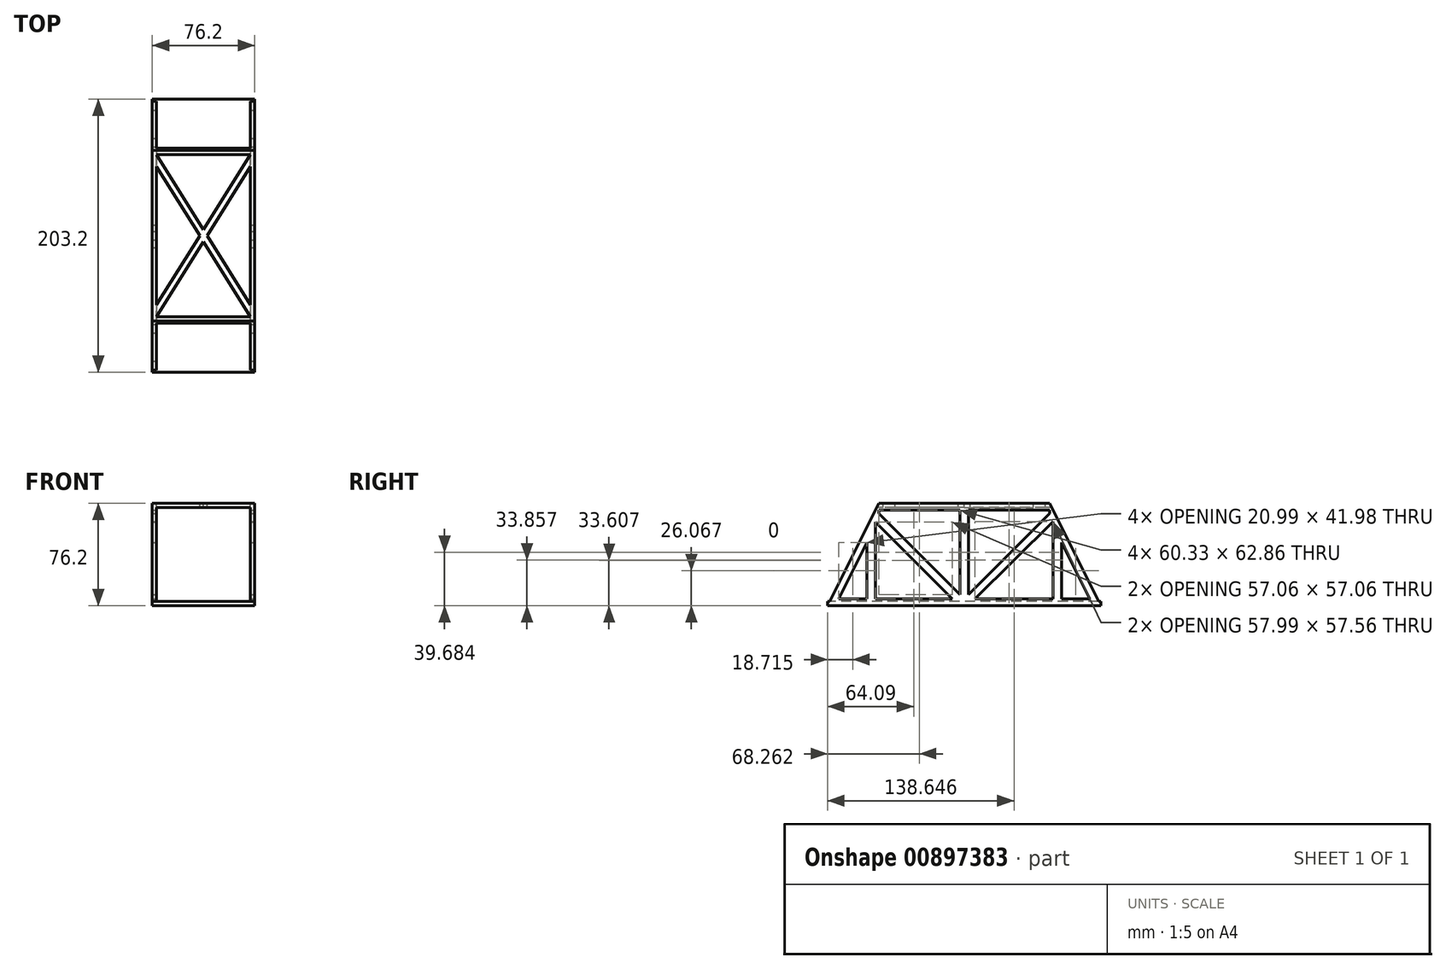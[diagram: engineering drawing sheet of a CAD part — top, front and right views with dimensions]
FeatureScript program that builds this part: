
annotation { "Feature Type Name" : "Feature", "Feature Type Description" : "" }
export const myFeature = defineFeature(function(context is Context, id is Id, definition is map)
    precondition{}
    {
        {
            var Q0;
            Q0=qCreatedBy(makeId("Right.planeOp"),FACE);
            var sketch = newSketch(context, id + "F0", { "sketchPlane" : qUnion([Q0])});
            skLineSegment(sketch, "E0", {"start": v(-101.6, -44.1) * mm, "end": v(101.6, -44.1) * mm});
            skLineSegment(sketch, "E1", {"start": v(-63.5, 32.1) * mm, "end": v(63.5, 32.1) * mm});
            skLineSegment(sketch, "E2", {"start": v(-101.6, -44.1) * mm, "end": v(-63.5, 32.1) * mm});
            skLineSegment(sketch, "E3", {"start": v(63.5, 32.1) * mm, "end": v(101.6, -44.1) * mm});
            skSolve(sketch);
        }
        {
            var Q0;
            Q0=makeQuery(id+"F0.imprint","IMPRINT",FACE,{"disambiguationData":[TD([[makeQuery(id+"F0.imprint","IMPRINT",EDGE,{"derivedFrom":sQuery(id+"F0.wireOp",EDGE,"E0")}),1.0]])]});
            extrude(context, id + "F1", {"entities" : qUnion([Q0]), "endBound" : BoundingType.SYMMETRIC, "depth" : 76.2 * mm, "offsetDistance" : 25.4 * mm});
        }
        {
            var Q0;
            Q0=qCreatedBy(makeId("Front.planeOp"),FACE);
            var sketch = newSketch(context, id + "F2", { "sketchPlane" : qUnion([Q0])});
            skLineSegment(sketch, "E4.bottom", {"start": v(34.92, -40.93) * mm, "end": v(-34.93, -40.93) * mm});
            skLineSegment(sketch, "E4.top", {"start": v(34.92, 28.92) * mm, "end": v(-34.92, 28.92) * mm});
            skLineSegment(sketch, "E4.left", {"start": v(34.93, -40.93) * mm, "end": v(34.93, 28.92) * mm});
            skLineSegment(sketch, "E4.right", {"start": v(-34.93, -40.93) * mm, "end": v(-34.93, 28.92) * mm});
            skPoint(sketch, "E4.middle", {"position": v(0, -6) * mm});
            skSolve(sketch);
        }
        {
            var Q0;
            Q0 = qSketchRegion(id + "F2", true);
            extrude(context, id + "F3", {"entities" : qUnion([Q0]), "operationType" : NewBodyOperationType.REMOVE, "endBound" : BoundingType.SYMMETRIC, "oppositeDirection" : true, "depth" : 254 * mm, "offsetDistance" : 25.4 * mm});
        }
        {
            var Q0;
            Q0=makeQuery(id+"F1.opExtrude","CAP_FACE",FACE,{"disambiguationData":[OSD([sQuery(id+"F0.wireOp",EDGE,"E0"),sQuery(id+"F0.wireOp",EDGE,"E1"),sQuery(id+"F0.wireOp",EDGE,"E2"),sQuery(id+"F0.wireOp",EDGE,"E3")])],"isStart":false});
            var sketch = newSketch(context, id + "F4", { "sketchPlane" : qUnion([Q0])});
            skLineSegment(sketch, "E5", {"start": v(-99.06, -39.02) * mm, "end": v(99.06, -39.02) * mm});
            skLineSegment(sketch, "E6", {"start": v(-66.04, 27.02) * mm, "end": v(66.04, 27.02) * mm});
            skLineSegment(sketch, "E7", {"start": v(-66.04, 27.02) * mm, "end": v(-66.04, -39.02) * mm});
            skLineSegment(sketch, "E8", {"start": v(66.04, 27.02) * mm, "end": v(66.04, -39.02) * mm});
            skLineSegment(sketch, "E9", {"start": v(-72.4, 14.32) * mm, "end": v(-72.4, -39.02) * mm});
            skLineSegment(sketch, "E10", {"start": v(72.39, 14.32) * mm, "end": v(72.39, -39.02) * mm});
            skLineSegment(sketch, "E11", {"start": v(72.39, 2.96) * mm, "end": v(93.38, -39.02) * mm});
            skLineSegment(sketch, "E12", {"start": v(-72.4, 2.96) * mm, "end": v(-93.38, -39.02) * mm});
            skLineSegment(sketch, "E13", {"start": v(-66.04, 27.02) * mm, "end": v(0, -39.02) * mm});
            skLineSegment(sketch, "E14", {"start": v(0, -39.02) * mm, "end": v(66.04, 27.02) * mm});
            skLineSegment(sketch, "E15", {"start": v(-66.04, 18.04) * mm, "end": v(-8, -40) * mm});
            skLineSegment(sketch, "E16", {"start": v(8.05, -39.02) * mm, "end": v(66.04, 18.54) * mm});
            skLineSegment(sketch, "E17", {"start": v(-3.18, 27.02) * mm, "end": v(-3.17, -35.85) * mm});
            skLineSegment(sketch, "E18", {"start": v(3.17, 27.02) * mm, "end": v(3.18, -35.85) * mm});
            skLineSegment(sketch, "E19", {"start": v(-63.5, 27.02) * mm, "end": v(-63.5, 24.48) * mm});
            skLineSegment(sketch, "E20", {"start": v(63.5, 27.02) * mm, "end": v(63.5, 24.48) * mm});
            skSolve(sketch);
        }
        {
            var Q0;
            {var subQ3=sQuery(id+"F4.wireOp",EDGE,"E12");Q0=makeQuery(id+"F4.imprint","IMPRINT",FACE,{"disambiguationData":[TD([[makeQuery(id+"F4.imprint","IMPRINT",EDGE,{"derivedFrom":subQ3}),1.0]])]});}
            var Q1;
            {var subQ0=sQuery(id+"F4.wireOp",EDGE,"E7");var subQ1=sQuery(id+"F4.wireOp",EDGE,"E5");var subQ2=makeQuery(id+"F4.imprint","INTERSECT",VERTEX,{"derivedFrom":[subQ1,subQ0]});Q1=makeQuery(id+"F4.imprint","IMPRINT",FACE,{"disambiguationData":[TD([[makeQuery(id+"F4.imprint","IMPRINT",EDGE,{"disambiguationData":[TD([[subQ2,-1.0]])],"derivedFrom":subQ1}),1.0]])]});}
            var Q2;
            {var subQ0=sQuery(id+"F4.wireOp",EDGE,"E17");Q2=makeQuery(id+"F4.imprint","IMPRINT",FACE,{"disambiguationData":[TD([[makeQuery(id+"F4.imprint","IMPRINT",EDGE,{"derivedFrom":subQ0}),-1.0]])]});}
            var Q3;
            {var subQ0=sQuery(id+"F4.wireOp",EDGE,"E18");Q3=makeQuery(id+"F4.imprint","IMPRINT",FACE,{"disambiguationData":[TD([[makeQuery(id+"F4.imprint","IMPRINT",EDGE,{"derivedFrom":subQ0}),1.0]])]});}
            var Q4;
            {var subQ3=sQuery(id+"F4.wireOp",EDGE,"E16");Q4=makeQuery(id+"F4.imprint","IMPRINT",FACE,{"disambiguationData":[TD([[makeQuery(id+"F4.imprint","IMPRINT",EDGE,{"derivedFrom":subQ3}),-1.0]])]});}
            var Q5;
            {var subQ3=sQuery(id+"F4.wireOp",EDGE,"E11");Q5=makeQuery(id+"F4.imprint","IMPRINT",FACE,{"disambiguationData":[TD([[makeQuery(id+"F4.imprint","IMPRINT",EDGE,{"derivedFrom":subQ3}),-1.0]])]});}
            extrude(context, id + "F5", {"entities" : qUnion([Q0, Q1, Q2, Q3, Q4, Q5]), "operationType" : NewBodyOperationType.REMOVE, "oppositeDirection" : true, "depth" : 76.2 * mm, "offsetDistance" : 25.4 * mm});
        }
        {
            var Q0;
            Q0=makeQuery(id+"F1.opExtrude","SWEPT_FACE",FACE,{"disambiguationData":[OSD([sQuery(id+"F0.wireOp",EDGE,"E1")])]});
            var sketch = newSketch(context, id + "F6", { "sketchPlane" : qUnion([Q0])});
            skLineSegment(sketch, "E21.bottom", {"start": v(34.92, -60.32) * mm, "end": v(-34.92, -60.33) * mm});
            skLineSegment(sketch, "E21.top", {"start": v(34.92, 60.33) * mm, "end": v(-34.92, 60.33) * mm});
            skLineSegment(sketch, "E21.left", {"start": v(34.92, -60.33) * mm, "end": v(34.92, 60.33) * mm});
            skLineSegment(sketch, "E21.right", {"start": v(-34.92, -60.33) * mm, "end": v(-34.92, 60.33) * mm});
            skPoint(sketch, "E21.middle", {"position": v(0, 0) * mm});
            skLineSegment(sketch, "E22", {"start": v(-34.92, 51.44) * mm, "end": v(34.93, -60.33) * mm});
            skLineSegment(sketch, "E23", {"start": v(-34.92, 60.33) * mm, "end": v(34.92, -51.44) * mm});
            skLineSegment(sketch, "E24", {"start": v(-34.93, -60.33) * mm, "end": v(34.93, 51.44) * mm});
            skLineSegment(sketch, "E25", {"start": v(-34.92, -51.44) * mm, "end": v(34.92, 60.33) * mm});
            skSolve(sketch);
        }
        {
            var Q0;
            {var subQ0=sQuery(id+"F6.wireOp",EDGE,"E22");var subQ1=sQuery(id+"F6.wireOp",EDGE,"E21.right");var subQ2=makeQuery(id+"F6.imprint","INTERSECT",VERTEX,{"derivedFrom":[subQ1,subQ0]});Q0=makeQuery(id+"F6.imprint","IMPRINT",FACE,{"disambiguationData":[TD([[makeQuery(id+"F6.imprint","IMPRINT",EDGE,{"disambiguationData":[TD([[subQ2,1.0]])],"derivedFrom":subQ1}),-1.0]])]});}
            var Q1;
            {var subQ0=sQuery(id+"F6.wireOp",EDGE,"E21.top");Q1=makeQuery(id+"F6.imprint","IMPRINT",FACE,{"disambiguationData":[TD([[makeQuery(id+"F6.imprint","IMPRINT",EDGE,{"derivedFrom":subQ0}),1.0]])]});}
            var Q2;
            {var subQ0=sQuery(id+"F6.wireOp",EDGE,"E23");var subQ1=sQuery(id+"F6.wireOp",EDGE,"E21.left");var subQ2=makeQuery(id+"F6.imprint","INTERSECT",VERTEX,{"derivedFrom":[subQ1,subQ0]});Q2=makeQuery(id+"F6.imprint","IMPRINT",FACE,{"disambiguationData":[TD([[makeQuery(id+"F6.imprint","IMPRINT",EDGE,{"disambiguationData":[TD([[subQ2,-1.0]])],"derivedFrom":subQ1}),1.0]])]});}
            var Q3;
            {var subQ0=sQuery(id+"F6.wireOp",EDGE,"E21.bottom");Q3=makeQuery(id+"F6.imprint","IMPRINT",FACE,{"disambiguationData":[TD([[makeQuery(id+"F6.imprint","IMPRINT",EDGE,{"derivedFrom":subQ0}),-1.0]])]});}
            extrude(context, id + "F7", {"entities" : qUnion([Q0, Q1, Q2, Q3]), "operationType" : NewBodyOperationType.REMOVE, "oppositeDirection" : true, "depth" : 5.6 * mm, "offsetDistance" : 25.4 * mm});
        }
        {
            var Q0;
            Q0=makeQuery(id+"F1.opExtrude","CAP_FACE",FACE,{"disambiguationData":[OSD([sQuery(id+"F0.wireOp",EDGE,"E0"),sQuery(id+"F0.wireOp",EDGE,"E1"),sQuery(id+"F0.wireOp",EDGE,"E2"),sQuery(id+"F0.wireOp",EDGE,"E3")])],"isStart":false});
            var sketch = newSketch(context, id + "F8", { "sketchPlane" : qUnion([Q0])});
            skLineSegment(sketch, "E26.bottom", {"start": v(-96.52, -40.93) * mm, "end": v(-101.6, -40.93) * mm});
            skLineSegment(sketch, "E26.top", {"start": v(-96.52, -44.1) * mm, "end": v(-101.6, -44.1) * mm});
            skLineSegment(sketch, "E26.left", {"start": v(-96.52, -40.93) * mm, "end": v(-96.52, -44.1) * mm});
            skLineSegment(sketch, "E26.right", {"start": v(-101.6, -40.93) * mm, "end": v(-101.6, -44.1) * mm});
            skLineSegment(sketch, "E27.MirrorCS", {"start": v(96.52, -40.93) * mm, "end": v(101.6, -40.93) * mm});
            skLineSegment(sketch, "E28.MirrorCS", {"start": v(96.52, -40.93) * mm, "end": v(96.52, -44.1) * mm});
            skLineSegment(sketch, "E29.MirrorCS", {"start": v(96.52, -44.1) * mm, "end": v(101.6, -44.1) * mm});
            skLineSegment(sketch, "E30.MirrorCS", {"start": v(101.6, -40.93) * mm, "end": v(101.6, -44.1) * mm});
            skSolve(sketch);
        }
        {
            var Q0;
            Q0 = qSketchRegion(id + "F8", true);
            extrude(context, id + "F9", {"entities" : qUnion([Q0]), "operationType" : NewBodyOperationType.ADD, "oppositeDirection" : true, "depth" : 76.2 * mm, "offsetDistance" : 25.4 * mm});
        }
    });
